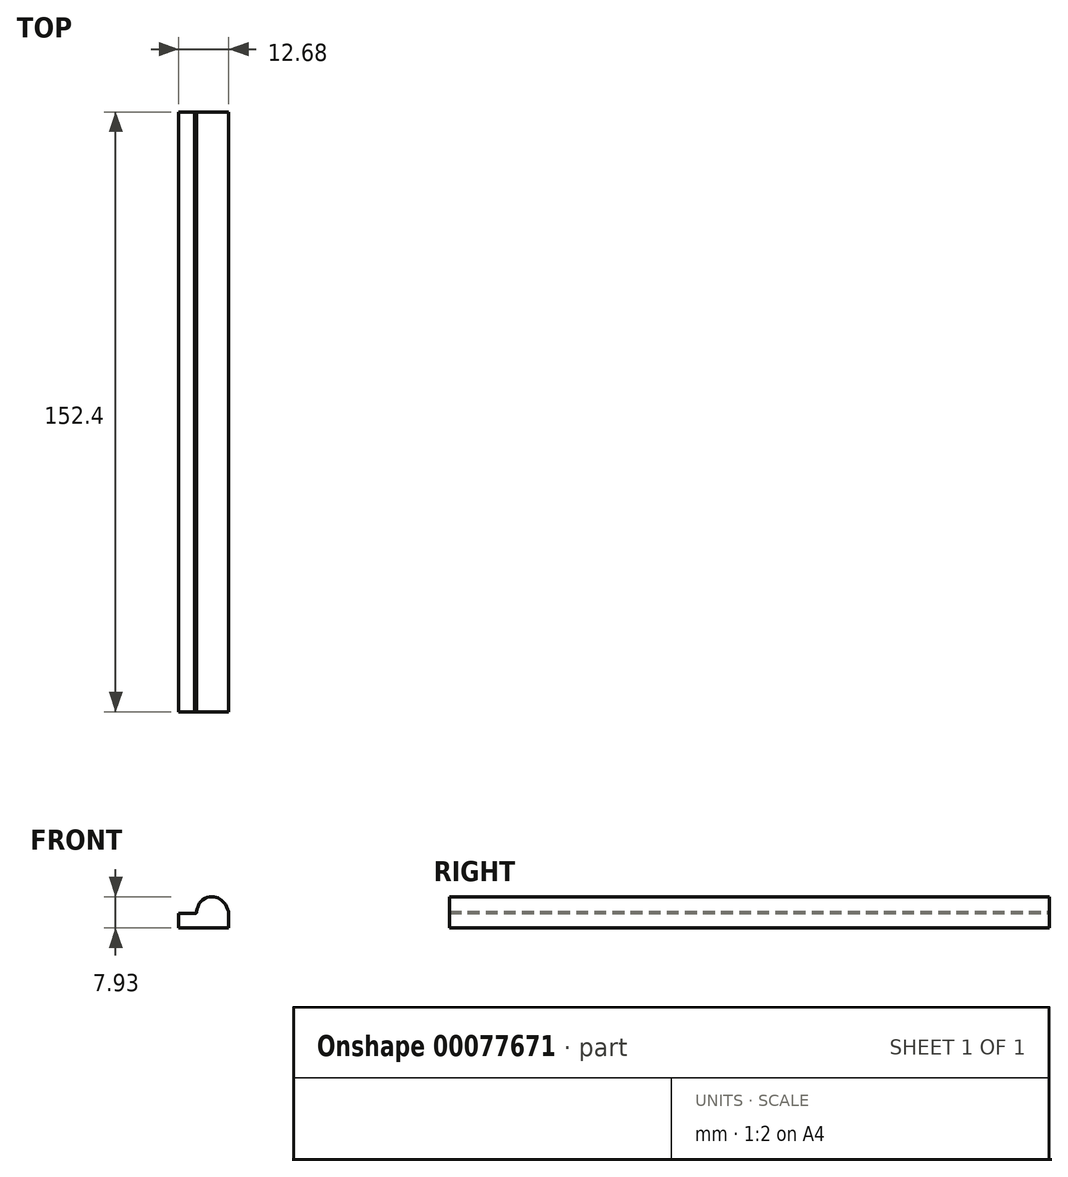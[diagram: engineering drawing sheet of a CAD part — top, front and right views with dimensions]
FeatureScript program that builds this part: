
annotation { "Feature Type Name" : "Feature", "Feature Type Description" : "" }
export const myFeature = defineFeature(function(context is Context, id is Id, definition is map)
    precondition{}
    {
        {
            var Q0;
            Q0=qCreatedBy(makeId("Front.planeOp"),FACE);
            var sketch = newSketch(context, id + "F0", { "sketchPlane" : qUnion([Q0])});
            skLineSegment(sketch, "E0", {"start": v(-2.37, -0.25) * mm, "end": v(-6.36, -0.25) * mm});
            skLineSegment(sketch, "E1", {"start": v(-6.36, -0.25) * mm, "end": v(-6.36, -3.96) * mm});
            skLineSegment(sketch, "E2", {"start": v(-6.36, -3.96) * mm, "end": v(6.3, -3.96) * mm});
            skLineSegment(sketch, "E3", {"start": v(6.3, -3.96) * mm, "end": v(6.3, -1.18) * mm});
            skFitSpline(sketch, "E4", {"points": [v(6.3, -1.18) * mm, v(6.3, -0.12) * mm, v(5.74, 1.6) * mm, v(4.23, 3.28) * mm, v(2.93, 3.9) * mm, v(1.39, 3.89) * mm, v(-0.42, 3.14) * mm, v(-1.32, 1.9) * mm, v(-1.78, 0.24) * mm], "startDerivative": vector(0, 10.98) * mm, "endDerivative": vector(-2.16, -15.64) * mm});
            skArc(sketch, "E5", {"start": v(-1.78, 0.24) * mm, "mid": v(-1.79, 0.14) * mm, "end": v(-1.82, 0.05) * mm});
            skArc(sketch, "E6", {"start": v(-1.82, 0.05) * mm, "mid": v(-2.05, -0.21) * mm, "end": v(-2.4, -0.25) * mm});
            skSolve(sketch);
        }
        {
            var Q0;
            {var subQ0=sQuery(id+"F0.wireOp",EDGE,"E1");Q0=makeQuery(id+"F0.imprint","IMPRINT",FACE,{"disambiguationData":[TD([[makeQuery(id+"F0.imprint","IMPRINT",EDGE,{"derivedFrom":subQ0}),1.0]])]});}
            extrude(context, id + "F1", {"entities" : qUnion([Q0]), "depth" : 152.4 * mm});
        }
    });
